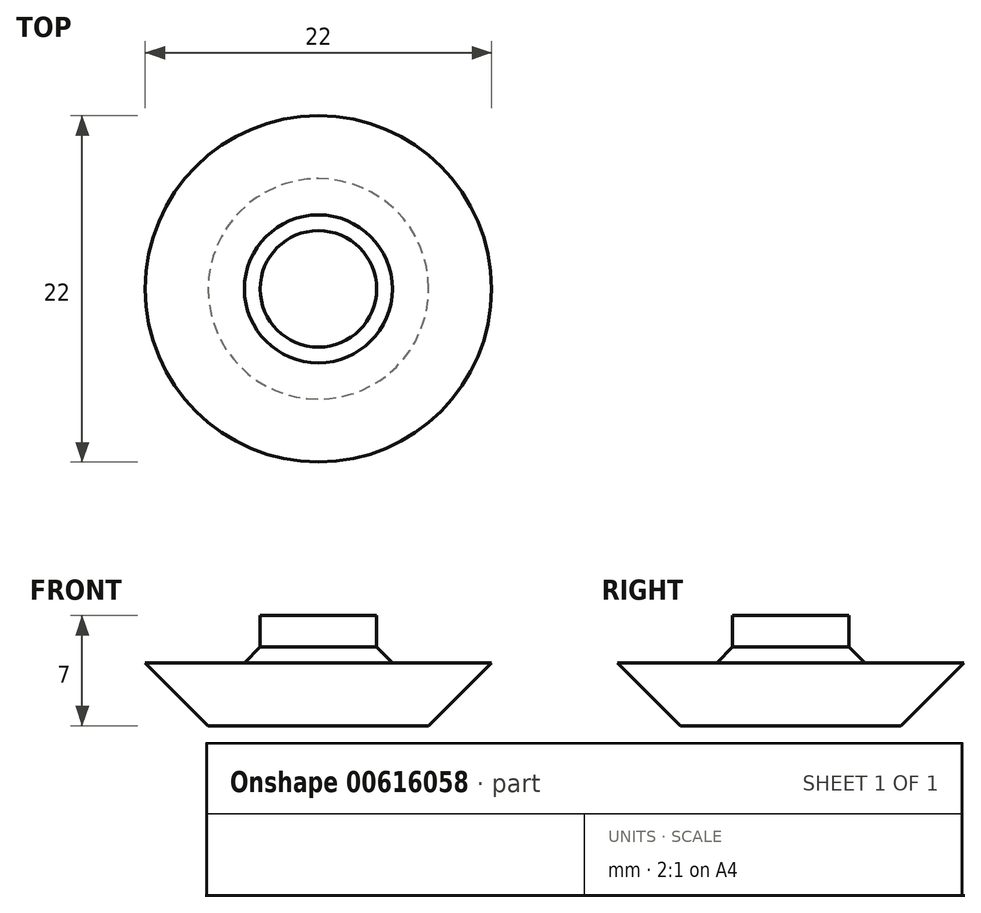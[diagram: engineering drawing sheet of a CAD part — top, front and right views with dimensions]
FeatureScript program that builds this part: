
annotation { "Feature Type Name" : "Feature", "Feature Type Description" : "" }
export const myFeature = defineFeature(function(context is Context, id is Id, definition is map)
    precondition{}
    {
        {
            var Q0;
            Q0=qCreatedBy(makeId("Top.planeOp"),FACE);
            var sketch = newSketch(context, id + "F0", { "sketchPlane" : qUnion([Q0])});
            skCircle(sketch, "E0", {"center": v(0, 0) * mm, "radius": 3.7 * mm});
            skCircle(sketch, "E1", {"center": v(0, 0) * mm, "radius": 11 * mm});
            skSolve(sketch);
        }
        {
            var Q0;
            Q0 = qSketchRegion(id + "F0", true);
            var Q1;
            Q1=makeQuery(id+"F0.imprint","IMPRINT",FACE,{"disambiguationData":[TD([[makeQuery(id+"F0.imprint","IMPRINT",EDGE,{"derivedFrom":sQuery(id+"F0.wireOp",EDGE,"E0")}),1.0]])]});
            extrude(context, id + "F1", {"entities" : qUnion([Q0, Q1]), "depth" : 4 * mm, "offsetDistance" : 25 * mm});
        }
        {
            var Q0;
            Q0=makeQuery(id+"F0.imprint","IMPRINT",FACE,{"disambiguationData":[TD([[makeQuery(id+"F0.imprint","IMPRINT",EDGE,{"derivedFrom":sQuery(id+"F0.wireOp",EDGE,"E0")}),1.0]])]});
            extrude(context, id + "F2", {"entities" : qUnion([Q0]), "operationType" : NewBodyOperationType.ADD, "depth" : 7 * mm, "offsetDistance" : 25 * mm});
        }
        {
            var Q0;
            Q0=makeQuery(id+"F1.opExtrude","CAP_FACE",FACE,{"disambiguationData":[OSD([sQuery(id+"F0.wireOp",EDGE,"E1")])],"isStart":true});
            chamfer(context, id + "F3", {"entities" : qUnion([Q0]), "width" : 4 * mm, "tangentPropagation" : true});
        }
        {
            var Q0;
            Q0=makeQuery(id+"F2.boolean.opBoolean","INTERSECT",EDGE,{"derivedFrom":[makeQuery(id+"F1.opExtrude","CAP_FACE",FACE,{"disambiguationData":[OSD([sQuery(id+"F0.wireOp",EDGE,"E1")])],"isStart":false}),makeQuery(id+"F2.opExtrude","SWEPT_FACE",FACE,{"disambiguationData":[OSD([sQuery(id+"F0.wireOp",EDGE,"E0")])]})]});
            chamfer(context, id + "F4", {"entities" : qUnion([Q0]), "width" : 1 * mm, "tangentPropagation" : true});
        }
    });
